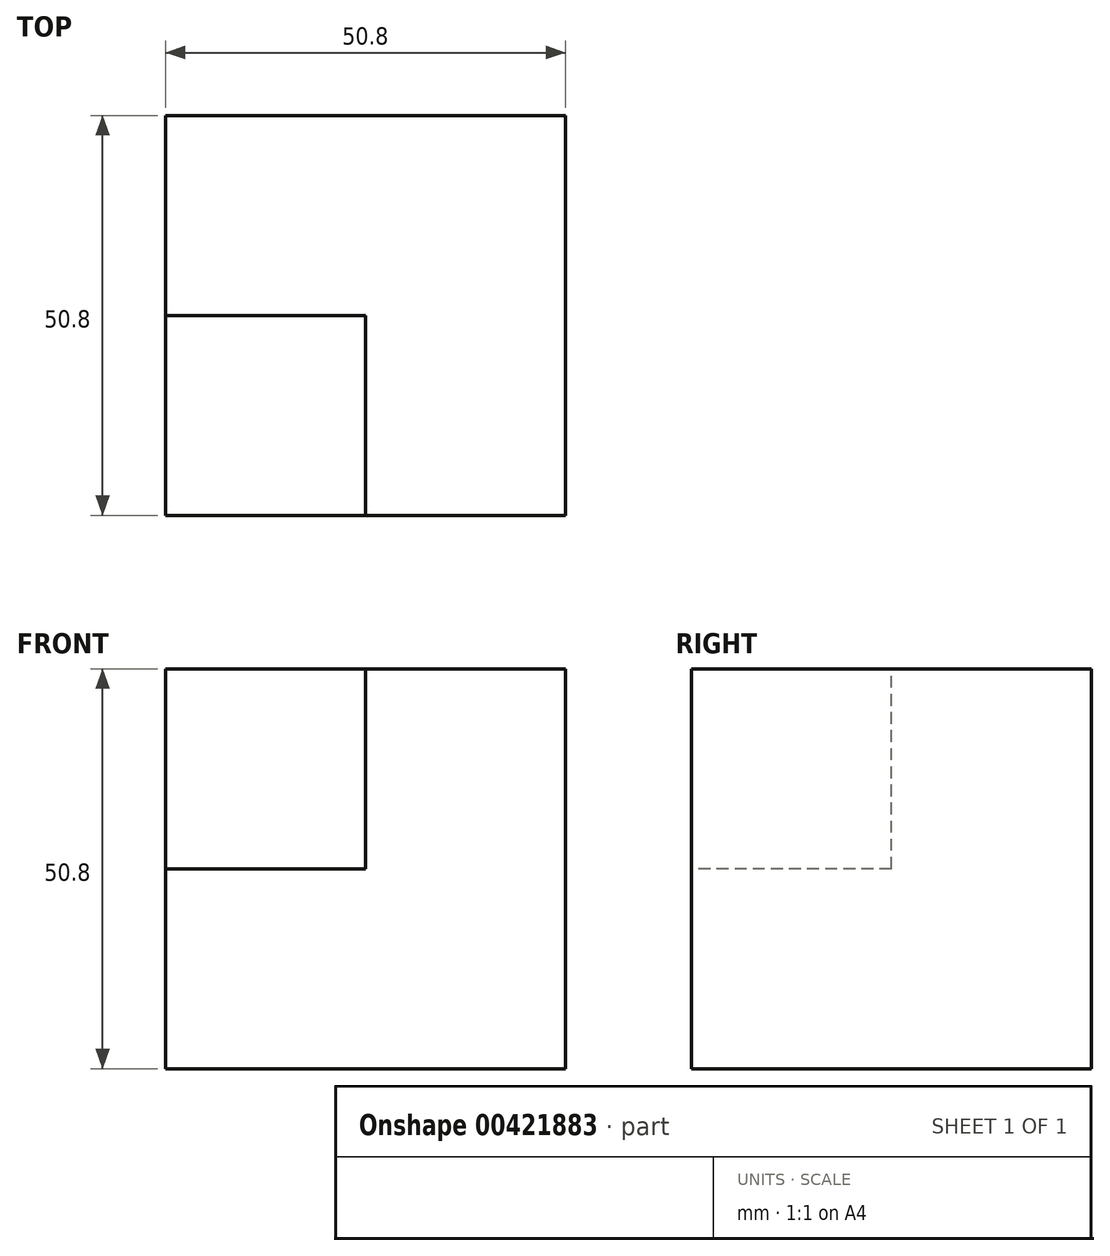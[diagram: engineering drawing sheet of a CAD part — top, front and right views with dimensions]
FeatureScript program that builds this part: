
annotation { "Feature Type Name" : "Feature", "Feature Type Description" : "" }
export const myFeature = defineFeature(function(context is Context, id is Id, definition is map)
    precondition{}
    {
        {
            var Q0;
            Q0=qCreatedBy(makeId("Front.planeOp"),FACE);
            var sketch = newSketch(context, id + "F0", { "sketchPlane" : qUnion([Q0])});
            skLineSegment(sketch, "E0.bottom", {"start": v(0, 0) * mm, "end": v(-50.8, 0) * mm});
            skLineSegment(sketch, "E0.top", {"start": v(0, 50.8) * mm, "end": v(-50.8, 50.8) * mm});
            skLineSegment(sketch, "E0.left", {"start": v(0, 0) * mm, "end": v(0, 50.8) * mm});
            skLineSegment(sketch, "E0.right", {"start": v(-50.8, 0) * mm, "end": v(-50.8, 50.8) * mm});
            skSolve(sketch);
        }
        {
            var Q0;
            Q0 = qSketchRegion(id + "F0", true);
            var Q1;
            Q1 = qSketchRegion(id + "F2", true);
            extrude(context, id + "F1", {"entities" : qUnion([Q0, Q1]), "depth" : 50.8 * mm});
        }
        {
            var Q0;
            Q0=makeQuery(id+"F1.opExtrude","CAP_FACE",FACE,{"disambiguationData":[OSD([sQuery(id+"F0.wireOp",EDGE,"E0.bottom"),sQuery(id+"F0.wireOp",EDGE,"E0.top"),sQuery(id+"F0.wireOp",EDGE,"E0.left"),sQuery(id+"F0.wireOp",EDGE,"E0.right")])],"isStart":false});
            var sketch = newSketch(context, id + "F2", { "sketchPlane" : qUnion([Q0])});
            skLineSegment(sketch, "E1.bottom", {"start": v(-50.8, 50.8) * mm, "end": v(-25.4, 50.8) * mm});
            skLineSegment(sketch, "E1.top", {"start": v(-50.8, 25.4) * mm, "end": v(-25.4, 25.4) * mm});
            skLineSegment(sketch, "E1.left", {"start": v(-50.8, 50.8) * mm, "end": v(-50.8, 25.4) * mm});
            skLineSegment(sketch, "E1.right", {"start": v(-25.4, 50.8) * mm, "end": v(-25.4, 25.4) * mm});
            skSolve(sketch);
        }
        {
            var Q0;
            Q0 = qSketchRegion(id + "F2", true);
            extrude(context, id + "F3", {"entities" : qUnion([Q0]), "operationType" : NewBodyOperationType.REMOVE, "oppositeDirection" : true, "depth" : 25.4 * mm});
        }
    });
